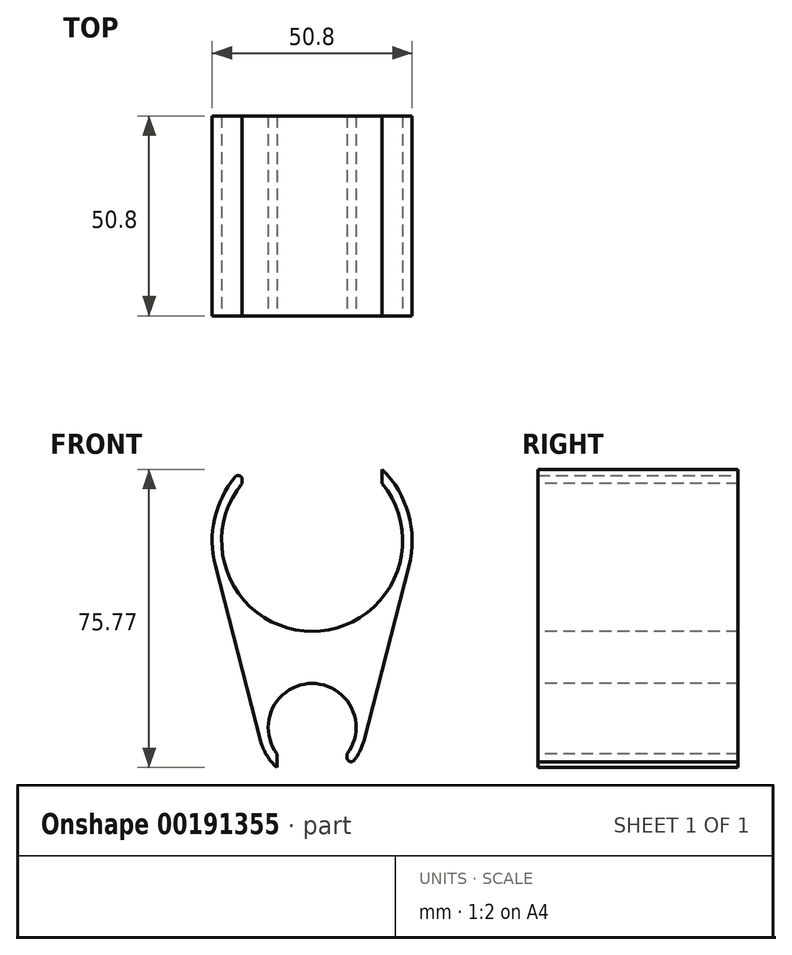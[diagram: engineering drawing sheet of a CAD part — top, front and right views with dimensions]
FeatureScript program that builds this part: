
annotation { "Feature Type Name" : "Feature", "Feature Type Description" : "" }
export const myFeature = defineFeature(function(context is Context, id is Id, definition is map)
    precondition{}
    {
        {
            var Q0;
            Q0=qCreatedBy(makeId("Front.planeOp"),FACE);
            var sketch = newSketch(context, id + "F0", { "sketchPlane" : qUnion([Q0])});
            skCircle(sketch, "E0", {"center": v(0, 0) * mm, "radius": 25.4 * mm, "construction": true});
            skLineSegment(sketch, "E1", {"start": v(0, 0) * mm, "end": v(0, -50.8) * mm, "construction": true});
            skLineSegment(sketch, "E2", {"start": v(-24.6, -6.35) * mm, "end": v(24.6, -6.35) * mm, "construction": true});
            skArc(sketch, "E3", {"start": v(-24.6, -6.35) * mm, "mid": v(0, 25.4) * mm, "end": v(24.6, -6.35) * mm});
            skLineSegment(sketch, "E4", {"start": v(-24.6, -6.35) * mm, "end": v(-13.12, -50.8) * mm});
            skLineSegment(sketch, "E5", {"start": v(24.6, -6.35) * mm, "end": v(13.12, -50.8) * mm});
            skLineSegment(sketch, "E6", {"start": v(-13.12, -50.8) * mm, "end": v(13.12, -50.8) * mm, "construction": true});
            skArc(sketch, "E7", {"start": v(-13.12, -50.8) * mm, "mid": v(0, -60.96) * mm, "end": v(13.12, -50.8) * mm});
            skCircle(sketch, "E8", {"center": v(0, -47.41) * mm, "radius": 13.47 * mm, "construction": true});
            skSolve(sketch);
        }
        {
            var Q0;
            Q0 = qSketchRegion(id + "F0", true);
            extrude(context, id + "F1", {"entities" : qUnion([Q0]), "depth" : 50.8 * mm});
        }
        {
            var Q0;
            Q0=makeQuery(id+"F1.opExtrude","CAP_FACE",FACE,{"disambiguationData":[OSD([sQuery(id+"F0.wireOp",EDGE,"E3"),sQuery(id+"F0.wireOp",EDGE,"E4"),sQuery(id+"F0.wireOp",EDGE,"E5"),sQuery(id+"F0.wireOp",EDGE,"E7")])],"isStart":false});
            var sketch = newSketch(context, id + "F2", { "sketchPlane" : qUnion([Q0])});
            skCircle(sketch, "E9", {"center": v(0, 0) * mm, "radius": 23 * mm});
            skCircle(sketch, "E10", {"center": v(0, -47.41) * mm, "radius": 11.15 * mm});
            skSolve(sketch);
        }
        {
            var Q0;
            Q0 = qSketchRegion(id + "F2", true);
            extrude(context, id + "F3", {"entities" : qUnion([Q0]), "operationType" : NewBodyOperationType.REMOVE, "endBound" : BoundingType.THROUGH_ALL, "oppositeDirection" : true, "depth" : 25.4 * mm});
        }
        {
            var Q0;
            Q0=makeQuery(id+"F1.opExtrude","CAP_FACE",FACE,{"disambiguationData":[OSD([sQuery(id+"F0.wireOp",EDGE,"E3"),sQuery(id+"F0.wireOp",EDGE,"E4"),sQuery(id+"F0.wireOp",EDGE,"E5"),sQuery(id+"F0.wireOp",EDGE,"E7")])],"isStart":false});
            var sketch = newSketch(context, id + "F4", { "sketchPlane" : qUnion([Q0])});
            skLineSegment(sketch, "E11.bottom", {"start": v(17.78, 2.45) * mm, "end": v(-17.78, 2.45) * mm});
            skLineSegment(sketch, "E11.top", {"start": v(17.78, 34.9) * mm, "end": v(-17.78, 34.9) * mm});
            skLineSegment(sketch, "E11.left", {"start": v(17.78, 2.45) * mm, "end": v(17.78, 34.9) * mm});
            skLineSegment(sketch, "E11.right", {"start": v(-17.78, 2.45) * mm, "end": v(-17.78, 34.9) * mm});
            skPoint(sketch, "E11.middle", {"position": v(0, 18.68) * mm});
            skLineSegment(sketch, "E12.bottom", {"start": v(8.89, -69.9) * mm, "end": v(-8.89, -69.9) * mm});
            skLineSegment(sketch, "E12.top", {"start": v(8.9, -47.22) * mm, "end": v(-8.89, -47.22) * mm});
            skLineSegment(sketch, "E12.left", {"start": v(8.9, -69.9) * mm, "end": v(8.9, -47.22) * mm});
            skLineSegment(sketch, "E12.right", {"start": v(-8.89, -69.9) * mm, "end": v(-8.89, -47.22) * mm});
            skPoint(sketch, "E12.middle", {"position": v(0, -58.56) * mm});
            skSolve(sketch);
        }
        {
            var Q0;
            {var subQ0=sQuery(id+"F4.wireOp",EDGE,"E11.left");var subQ1=makeQuery(id+"F1.opExtrude","CAP_EDGE",EDGE,{"disambiguationData":[OSD([sQuery(id+"F0.wireOp",EDGE,"E3")])],"isStart":false});var subQ2=makeQuery(id+"F4.imprint","INTERSECT",VERTEX,{"derivedFrom":[subQ1,subQ0]});Q0=makeQuery(id+"F4.imprint","IMPRINT",FACE,{"disambiguationData":[TD([[makeQuery(id+"F4.imprint","IMPRINT",EDGE,{"disambiguationData":[TD([[subQ2,1.0]])],"derivedFrom":subQ0}),1.0]])]});}
            var Q1;
            {var subQ0=sQuery(id+"F4.wireOp",EDGE,"E12.left");var subQ1=makeQuery(id+"F1.opExtrude","CAP_EDGE",EDGE,{"disambiguationData":[OSD([sQuery(id+"F0.wireOp",EDGE,"E7")])],"isStart":false});var subQ2=makeQuery(id+"F4.imprint","INTERSECT",VERTEX,{"derivedFrom":[subQ1,subQ0]});Q1=makeQuery(id+"F4.imprint","IMPRINT",FACE,{"disambiguationData":[TD([[makeQuery(id+"F4.imprint","IMPRINT",EDGE,{"disambiguationData":[TD([[subQ2,-1.0]])],"derivedFrom":subQ0}),1.0]])]});}
            extrude(context, id + "F5", {"entities" : qUnion([Q0, Q1]), "operationType" : NewBodyOperationType.REMOVE, "endBound" : BoundingType.THROUGH_ALL, "oppositeDirection" : true, "depth" : 25.4 * mm});
        }
        {
            var Q0;
            Q0=makeQuery(id+"F5.boolean.opBoolean","COPY",EDGE,{"derivedFrom":makeQuery(id+"F5.opExtrude","SWEPT_EDGE",EDGE,{"disambiguationData":[OSD([sQuery(id+"F0.wireOp",EDGE,"E3"),sQuery(id+"F4.wireOp",EDGE,"E11.left")])]})});
            var Q1;
            Q1=makeQuery(id+"F5.boolean.opBoolean","COPY",EDGE,{"derivedFrom":makeQuery(id+"F5.opExtrude","SWEPT_EDGE",EDGE,{"disambiguationData":[OSD([sQuery(id+"F0.wireOp",EDGE,"E3"),sQuery(id+"F4.wireOp",EDGE,"E11.right")])]})});
            var Q2;
            Q2=makeQuery(id+"F5.boolean.opBoolean","COPY",EDGE,{"derivedFrom":makeQuery(id+"F5.opExtrude","SWEPT_EDGE",EDGE,{"disambiguationData":[OSD([sQuery(id+"F0.wireOp",EDGE,"E7"),sQuery(id+"F4.wireOp",EDGE,"E12.left")])]})});
            var Q3;
            Q3=makeQuery(id+"F5.boolean.opBoolean","COPY",EDGE,{"derivedFrom":makeQuery(id+"F5.opExtrude","SWEPT_EDGE",EDGE,{"disambiguationData":[OSD([sQuery(id+"F0.wireOp",EDGE,"E7"),sQuery(id+"F4.wireOp",EDGE,"E12.right")])]})});
            fillet(context, id + "F6", {"entities" : qUnion([Q0, Q1, Q2, Q3]), "radius" : 1 * mm, "tangentPropagation" : true, "allowEdgeOverflow" : false});
        }
    });
